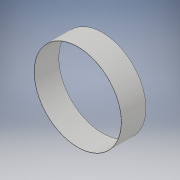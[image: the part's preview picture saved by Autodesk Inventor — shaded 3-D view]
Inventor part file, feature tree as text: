
AUTODESK INVENTOR PART (.ipt)
format: ipt  version: 2019 (Build 230136000, 136)  size: 104,960 bytes
history: native  units: mm
features: extrude x2, sketch x2
ambient origin geometry x8: Origin, YZ Plane, XZ Plane, XY Plane, X Axis, Y Axis, Z Axis, Center Point
bodies: Solid1 (feature_tree)
feature tree (4):
  extrude  "Extrusion1"  Depth=11.65mm TaperAngle=0.0deg
  extrude  "Extrusion2"  Depth=11.65mm TaperAngle=0.0deg
  sketch  "Sketch1"  dims[d0=41.668mm d1=11.65mm d2=0.0mm]
  sketch  "Sketch2"  dims[d3=41.4mm d4=11.65mm d5=0.0mm]
